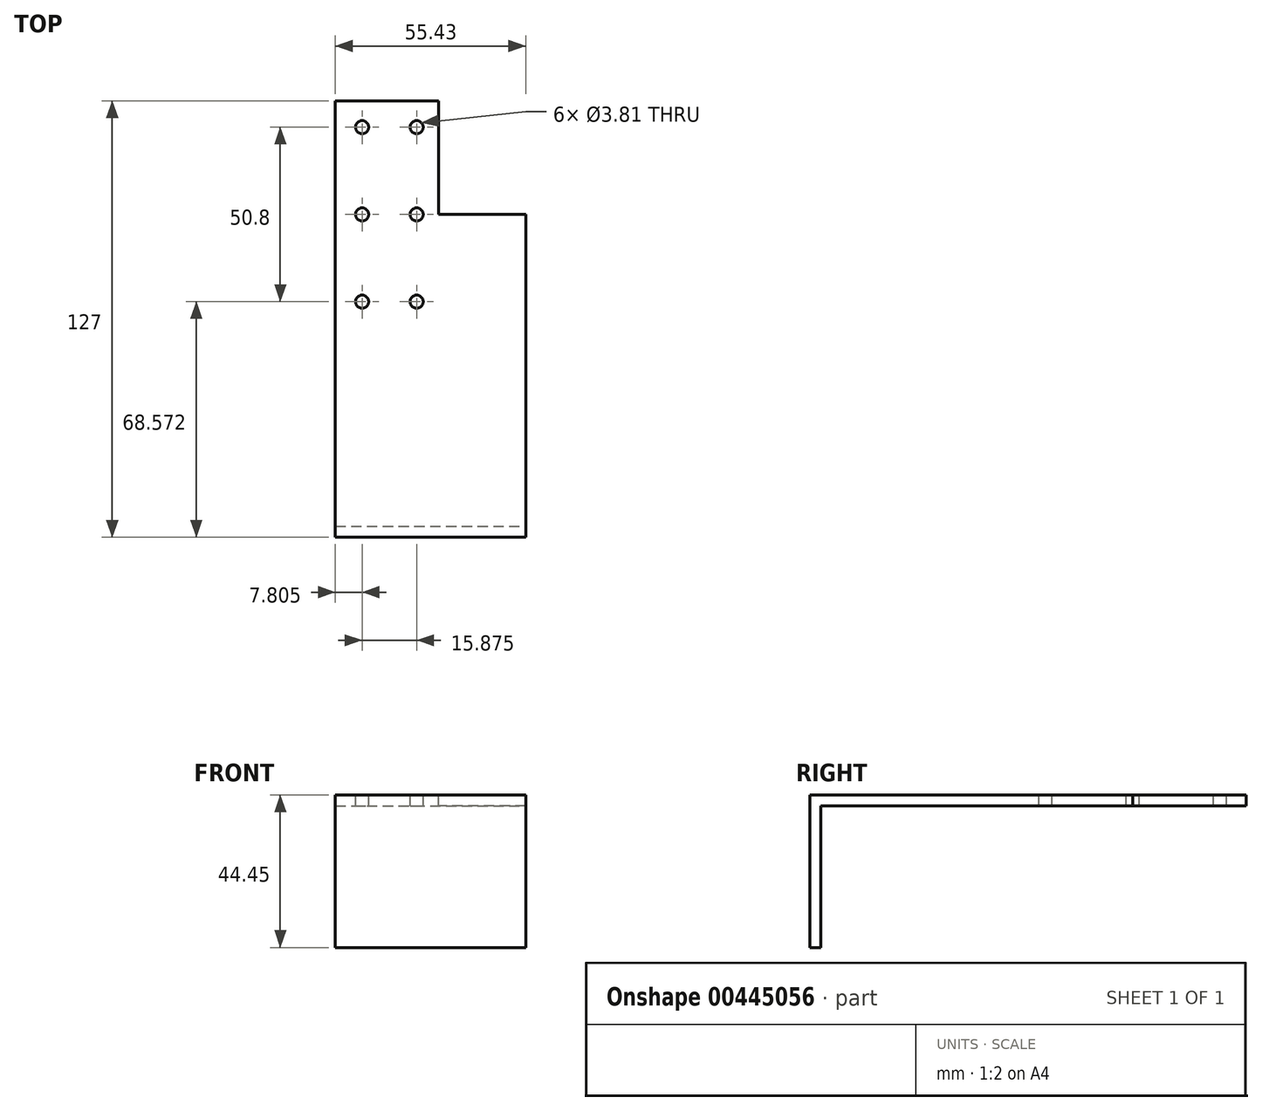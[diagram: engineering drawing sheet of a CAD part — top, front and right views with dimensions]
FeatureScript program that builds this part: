
annotation { "Feature Type Name" : "Feature", "Feature Type Description" : "" }
export const myFeature = defineFeature(function(context is Context, id is Id, definition is map)
    precondition{}
    {
        {
            var Q0;
            Q0=qCreatedBy(makeId("Right.planeOp"),FACE);
            var sketch = newSketch(context, id + "F0", { "sketchPlane" : qUnion([Q0])});
            skLineSegment(sketch, "E0.bottom", {"start": v(-108.33, 6.35) * mm, "end": v(15.5, 6.35) * mm});
            skLineSegment(sketch, "E0.top", {"start": v(-111.5, 9.52) * mm, "end": v(15.5, 9.52) * mm});
            skLineSegment(sketch, "E0.right", {"start": v(15.5, 6.35) * mm, "end": v(15.5, 9.52) * mm});
            skLineSegment(sketch, "E1.top", {"start": v(-111.5, -34.93) * mm, "end": v(-108.33, -34.93) * mm});
            skLineSegment(sketch, "E1.left", {"start": v(-111.5, 9.52) * mm, "end": v(-111.5, -34.93) * mm});
            skLineSegment(sketch, "E1.right", {"start": v(-108.33, 6.35) * mm, "end": v(-108.33, -34.93) * mm});
            skSolve(sketch);
        }
        {
            var Q0;
            Q0 = qSketchRegion(id + "F0", true);
            extrude(context, id + "F1", {"entities" : qUnion([Q0]), "oppositeDirection" : true, "depth" : 55.43 * mm});
        }
        {
            var Q0;
            Q0=makeQuery(id+"F1.opExtrude","SWEPT_FACE",FACE,{"disambiguationData":[OSD([sQuery(id+"F0.wireOp",EDGE,"E0.top")])]});
            var sketch = newSketch(context, id + "F2", { "sketchPlane" : qUnion([Q0])});
            skCircle(sketch, "E2", {"center": v(-47.62, 7.86) * mm, "radius": 1.9 * mm});
            skCircle(sketch, "E3", {"center": v(-47.62, -17.54) * mm, "radius": 1.9 * mm});
            skCircle(sketch, "E4", {"center": v(-47.62, -42.94) * mm, "radius": 1.9 * mm});
            skCircle(sketch, "E5.MirrorC", {"center": v(-31.75, -42.94) * mm, "radius": 1.9 * mm});
            skCircle(sketch, "E6.MirrorC", {"center": v(-31.75, -17.54) * mm, "radius": 1.9 * mm});
            skCircle(sketch, "E7.MirrorC", {"center": v(-31.75, 7.86) * mm, "radius": 1.9 * mm});
            skLineSegment(sketch, "E8", {"start": v(-25.4, 18.05) * mm, "end": v(-25.4, -17.54) * mm});
            skLineSegment(sketch, "E9", {"start": v(-25.4, -17.54) * mm, "end": v(0, -17.54) * mm});
            skLineSegment(sketch, "E10", {"start": v(-25.4, 18.05) * mm, "end": v(0, 18.05) * mm});
            skLineSegment(sketch, "E11", {"start": v(0, 18.05) * mm, "end": v(0, -17.54) * mm});
            skSolve(sketch);
        }
        {
            var Q0;
            Q0 = qSketchRegion(id + "F2", true);
            extrude(context, id + "F3", {"entities" : qUnion([Q0]), "operationType" : NewBodyOperationType.REMOVE, "oppositeDirection" : true, "depth" : 25.4 * mm});
        }
    });
